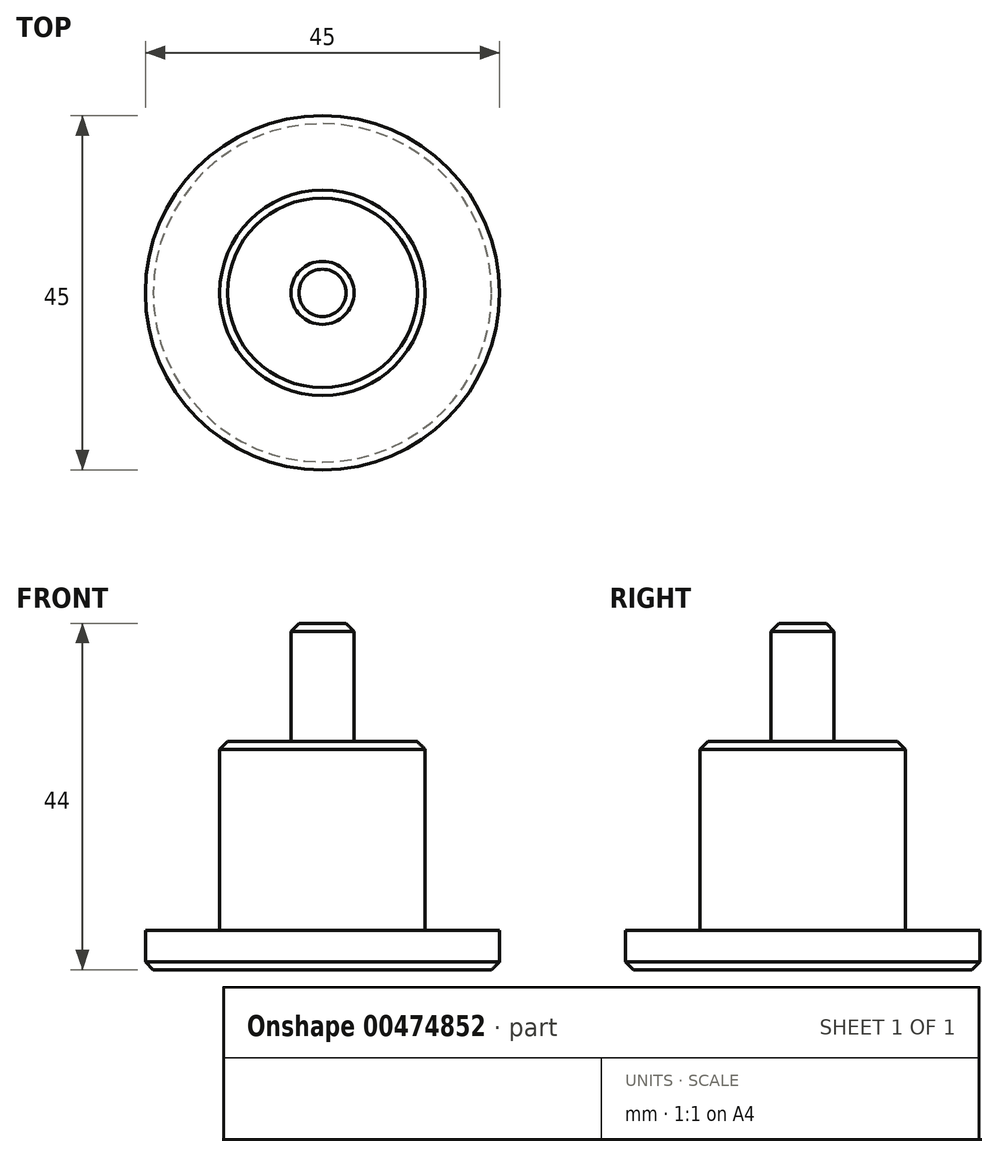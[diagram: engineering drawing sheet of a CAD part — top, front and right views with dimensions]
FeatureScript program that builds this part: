
annotation { "Feature Type Name" : "Feature", "Feature Type Description" : "" }
export const myFeature = defineFeature(function(context is Context, id is Id, definition is map)
    precondition{}
    {
        {
            var Q0;
            Q0=qCreatedBy(makeId("Top.planeOp"),FACE);
            var sketch = newSketch(context, id + "F0", { "sketchPlane" : qUnion([Q0])});
            skCircle(sketch, "E0", {"center": v(0, 0) * mm, "radius": 22.5 * mm});
            skSolve(sketch);
        }
        {
            var Q0;
            Q0=makeQuery(id+"F0.imprint","IMPRINT",FACE,{"disambiguationData":[TD([[makeQuery(id+"F0.imprint","IMPRINT",EDGE,{"derivedFrom":sQuery(id+"F0.wireOp",EDGE,"E0")}),1.0]])]});
            var Q1;
            Q1=makeQuery(id+"F0.imprint","IMPRINT",FACE,{"disambiguationData":[TD([[makeQuery(id+"F0.imprint","IMPRINT",EDGE,{"derivedFrom":sQuery(id+"F0.wireOp",EDGE,"GHQiRZfm-h0C7-2TbN-OvYM-QCjUTQap5qrz")}),1.0]])]});
            extrude(context, id + "F1", {"entities" : qUnion([Q0, Q1]), "depth" : 5 * mm});
        }
        {
            var Q0;
            Q0=qCreatedBy(makeId("Top.planeOp"),FACE);
            var sketch = newSketch(context, id + "F2", { "sketchPlane" : qUnion([Q0])});
            skCircle(sketch, "E1", {"center": v(0, 0) * mm, "radius": 13.05 * mm});
            skSolve(sketch);
        }
        {
            var Q0;
            Q0 = qSketchRegion(id + "F2", true);
            extrude(context, id + "F3", {"entities" : qUnion([Q0]), "operationType" : NewBodyOperationType.ADD, "depth" : 29 * mm});
        }
        {
            var Q0;
            Q0=qCreatedBy(makeId("Top.planeOp"),FACE);
            var sketch = newSketch(context, id + "F4", { "sketchPlane" : qUnion([Q0])});
            skCircle(sketch, "E2", {"center": v(0, 0) * mm, "radius": 4 * mm});
            skSolve(sketch);
        }
        {
            var Q0;
            Q0 = qSketchRegion(id + "F4", true);
            extrude(context, id + "F5", {"entities" : qUnion([Q0]), "operationType" : NewBodyOperationType.ADD, "depth" : 44 * mm});
        }
        {
            var Q0;
            Q0=makeQuery(id+"F1.opExtrude","CAP_EDGE",EDGE,{"disambiguationData":[OSD([sQuery(id+"F0.wireOp",EDGE,"E0")])],"isStart":true});
            var Q1;
            Q1=makeQuery(id+"F3.opExtrude","CAP_EDGE",EDGE,{"disambiguationData":[OSD([sQuery(id+"F2.wireOp",EDGE,"E1")])],"isStart":false});
            var Q2;
            Q2=makeQuery(id+"F5.opExtrude","CAP_EDGE",EDGE,{"disambiguationData":[OSD([sQuery(id+"F4.wireOp",EDGE,"E2")])],"isStart":false});
            chamfer(context, id + "F6", {"entities" : qUnion([Q0, Q1, Q2]), "width" : 1 * mm, "tangentPropagation" : true});
        }
    });
